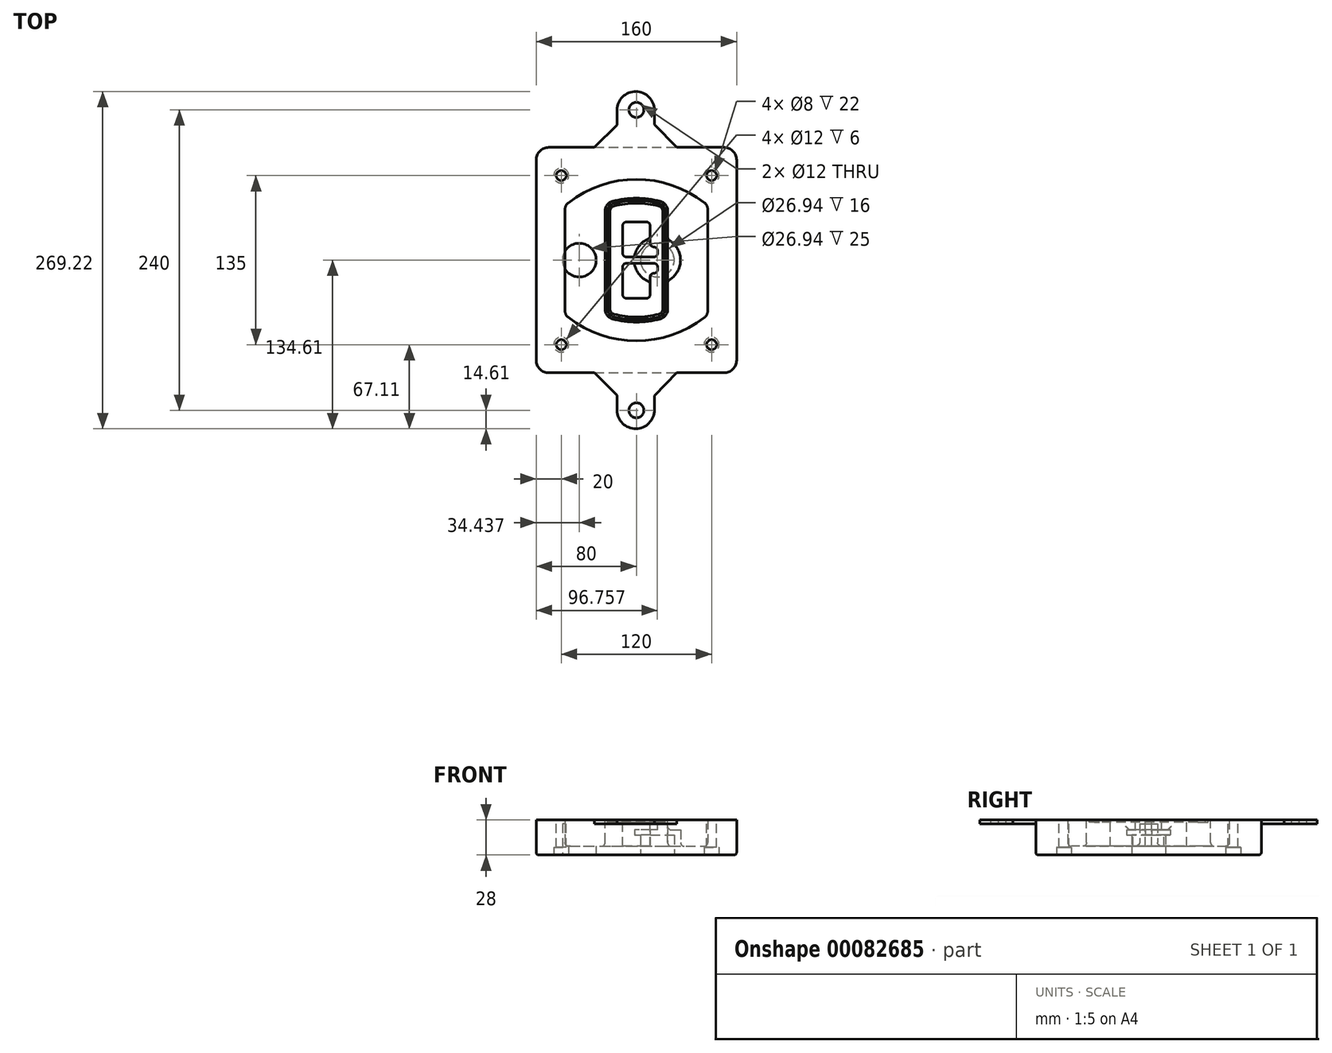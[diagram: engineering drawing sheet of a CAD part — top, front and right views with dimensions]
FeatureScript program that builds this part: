
annotation { "Feature Type Name" : "Feature", "Feature Type Description" : "" }
export const myFeature = defineFeature(function(context is Context, id is Id, definition is map)
    precondition{}
    {
        {
            var Q0;
            Q0=qCreatedBy(makeId("Top.planeOp"),FACE);
            var sketch = newSketch(context, id + "F0", { "sketchPlane" : qUnion([Q0])});
            skPoint(sketch, "E0.rect.middle", {"position": v(0, 0) * mm});
            skLineSegment(sketch, "E1.bottom", {"start": v(-70, -90) * mm, "end": v(70, -90) * mm});
            skLineSegment(sketch, "E1.top", {"start": v(-70, 90) * mm, "end": v(70, 90) * mm});
            skLineSegment(sketch, "E1.left", {"start": v(-80, -80) * mm, "end": v(-80, 80) * mm});
            skLineSegment(sketch, "E1.right", {"start": v(80, -80) * mm, "end": v(80, 80) * mm});
            skLineSegment(sketch, "E2", {"start": v(-80, 90) * mm, "end": v(80, -90) * mm, "construction": true});
            skLineSegment(sketch, "E3", {"start": v(80, 90) * mm, "end": v(-80, -90) * mm, "construction": true});
            skCircle(sketch, "E4", {"center": v(-60, 67.5) * mm, "radius": 4 * mm});
            skCircle(sketch, "E5", {"center": v(60, 67.5) * mm, "radius": 4 * mm});
            skCircle(sketch, "E6", {"center": v(60, -67.5) * mm, "radius": 4 * mm});
            skCircle(sketch, "E7", {"center": v(-60, -67.5) * mm, "radius": 4 * mm});
            skLineSegment(sketch, "E8", {"start": v(-60, 67.5) * mm, "end": v(60, 67.5) * mm, "construction": true});
            skLineSegment(sketch, "E9", {"start": v(60, 67.5) * mm, "end": v(60, -67.5) * mm, "construction": true});
            skLineSegment(sketch, "E10", {"start": v(60, -67.5) * mm, "end": v(-60, -67.5) * mm, "construction": true});
            skLineSegment(sketch, "E11", {"start": v(-60, -67.5) * mm, "end": v(-60, 67.5) * mm, "construction": true});
            skLineSegment(sketch, "E12", {"start": v(-60, 40.3) * mm, "end": v(-60, -40.3) * mm});
            skLineSegment(sketch, "E13", {"start": v(60, 40.3) * mm, "end": v(60, -40.3) * mm});
            skArc(sketch, "E14", {"start": v(56.15, 48.18) * mm, "mid": v(0, 67.5) * mm, "end": v(-56.15, 48.18) * mm});
            skArc(sketch, "E15", {"start": v(-56.15, -48.18) * mm, "mid": v(0, -67.5) * mm, "end": v(56.15, -48.18) * mm});
            skLineSegment(sketch, "E16", {"start": v(-60, 0) * mm, "end": v(60, 0) * mm, "construction": true});
            skPoint(sketch, "E17.visualSharp", {"position": v(-60, -45) * mm});
            skArc(sketch, "E17.filletArc", {"start": v(-60, -40.3) * mm, "mid": v(-58.99, -44.68) * mm, "end": v(-56.15, -48.18) * mm});
            skPoint(sketch, "E18.visualSharp", {"position": v(-60, 45) * mm});
            skArc(sketch, "E18.filletArc", {"start": v(-56.15, 48.18) * mm, "mid": v(-58.99, 44.68) * mm, "end": v(-60, 40.3) * mm});
            skPoint(sketch, "E19.visualSharp", {"position": v(60, 45) * mm});
            skArc(sketch, "E19.filletArc", {"start": v(60, 40.3) * mm, "mid": v(58.99, 44.68) * mm, "end": v(56.15, 48.18) * mm});
            skPoint(sketch, "E20.visualSharp", {"position": v(60, -45) * mm});
            skArc(sketch, "E20.filletArc", {"start": v(56.15, -48.18) * mm, "mid": v(58.99, -44.68) * mm, "end": v(60, -40.3) * mm});
            skPoint(sketch, "E21.visualSharp", {"position": v(-80, 90) * mm});
            skArc(sketch, "E21.filletArc", {"start": v(-70, 90) * mm, "mid": v(-77.07, 87.07) * mm, "end": v(-80, 80) * mm});
            skPoint(sketch, "E22.visualSharp", {"position": v(80, 90) * mm});
            skArc(sketch, "E22.filletArc", {"start": v(80, 80) * mm, "mid": v(77.07, 87.07) * mm, "end": v(70, 90) * mm});
            skPoint(sketch, "E23.visualSharp", {"position": v(80, -90) * mm});
            skArc(sketch, "E23.filletArc", {"start": v(70, -90) * mm, "mid": v(77.07, -87.07) * mm, "end": v(80, -80) * mm});
            skPoint(sketch, "E24.visualSharp", {"position": v(-80, -90) * mm});
            skArc(sketch, "E24.filletArc", {"start": v(-80, -80) * mm, "mid": v(-77.07, -87.07) * mm, "end": v(-70, -90) * mm});
            skArc(sketch, "E25.0", {"start": v(57, 40.3) * mm, "mid": v(56.3, 43.36) * mm, "end": v(54.3, 45.81) * mm});
            skLineSegment(sketch, "E25.1", {"start": v(57, 40.3) * mm, "end": v(57, -40.3) * mm});
            skArc(sketch, "E25.2", {"start": v(54.3, -45.81) * mm, "mid": v(56.3, -43.36) * mm, "end": v(57, -40.3) * mm});
            skArc(sketch, "E25.3", {"start": v(-54.3, -45.81) * mm, "mid": v(0, -64.5) * mm, "end": v(54.3, -45.81) * mm});
            skArc(sketch, "E25.4", {"start": v(-57, -40.3) * mm, "mid": v(-56.3, -43.36) * mm, "end": v(-54.3, -45.81) * mm});
            skArc(sketch, "E25.5", {"start": v(54.3, 45.81) * mm, "mid": v(0, 64.5) * mm, "end": v(-54.3, 45.81) * mm});
            skLineSegment(sketch, "E25.6", {"start": v(-57, 40.3) * mm, "end": v(-57, -40.3) * mm});
            skArc(sketch, "E25.7", {"start": v(-54.3, 45.81) * mm, "mid": v(-56.3, 43.36) * mm, "end": v(-57, 40.3) * mm});
            skArc(sketch, "E26.0", {"start": v(-58.62, 51.33) * mm, "mid": v(-62.58, 46.43) * mm, "end": v(-64, 40.3) * mm});
            skArc(sketch, "E26.1", {"start": v(58.62, 51.33) * mm, "mid": v(0, 71.5) * mm, "end": v(-58.62, 51.33) * mm});
            skArc(sketch, "E26.2", {"start": v(64, 40.3) * mm, "mid": v(62.58, 46.43) * mm, "end": v(58.62, 51.33) * mm});
            skLineSegment(sketch, "E26.3", {"start": v(64, 40.3) * mm, "end": v(64, -40.3) * mm});
            skArc(sketch, "E26.4", {"start": v(58.62, -51.33) * mm, "mid": v(62.58, -46.43) * mm, "end": v(64, -40.3) * mm});
            skLineSegment(sketch, "E26.5", {"start": v(-64, 40.3) * mm, "end": v(-64, -40.3) * mm});
            skArc(sketch, "E26.6", {"start": v(-58.62, -51.33) * mm, "mid": v(0, -71.5) * mm, "end": v(58.62, -51.33) * mm});
            skArc(sketch, "E26.7", {"start": v(-64, -40.3) * mm, "mid": v(-62.58, -46.43) * mm, "end": v(-58.62, -51.33) * mm});
            skSolve(sketch);
        }
        {
            var Q0;
            Q0=makeQuery(id+"F0.imprint","IMPRINT",FACE,{"disambiguationData":[TD([[makeQuery(id+"F0.imprint","IMPRINT",EDGE,{"derivedFrom":sQuery(id+"F0.wireOp",EDGE,"E1.bottom")}),1.0]])]});
            var Q1;
            Q1=makeQuery(id+"F0.imprint","IMPRINT",FACE,{"disambiguationData":[TD([[makeQuery(id+"F0.imprint","IMPRINT",EDGE,{"derivedFrom":sQuery(id+"F0.wireOp",EDGE,"E12")}),1.0]])]});
            var Q2;
            Q2=makeQuery(id+"F0.imprint","IMPRINT",FACE,{"disambiguationData":[TD([[makeQuery(id+"F0.imprint","IMPRINT",EDGE,{"derivedFrom":sQuery(id+"F0.wireOp",EDGE,"E25.0")}),1.0]])]});
            var Q3;
            Q3=makeQuery(id+"F0.imprint","IMPRINT",FACE,{"disambiguationData":[TD([[makeQuery(id+"F0.imprint","IMPRINT",EDGE,{"derivedFrom":sQuery(id+"F0.wireOp",EDGE,"E12")}),-1.0]])]});
            extrude(context, id + "F1", {"entities" : qUnion([Q0, Q1, Q2, Q3]), "oppositeDirection" : true, "depth" : 25 * mm});
        }
        {
            var Q0;
            Q0=makeQuery(id+"F0.imprint","IMPRINT",FACE,{"disambiguationData":[TD([[makeQuery(id+"F0.imprint","IMPRINT",EDGE,{"derivedFrom":sQuery(id+"F0.wireOp",EDGE,"E12")}),1.0]])]});
            extrude(context, id + "F2", {"entities" : qUnion([Q0]), "operationType" : NewBodyOperationType.ADD, "depth" : 3 * mm});
        }
        {
            var Q0;
            Q0=makeQuery(id+"F0.imprint","IMPRINT",FACE,{"disambiguationData":[TD([[makeQuery(id+"F0.imprint","IMPRINT",EDGE,{"derivedFrom":sQuery(id+"F0.wireOp",EDGE,"E25.0")}),1.0]])]});
            extrude(context, id + "F3", {"entities" : qUnion([Q0]), "operationType" : NewBodyOperationType.REMOVE, "oppositeDirection" : true, "depth" : 18 * mm});
        }
        {
            var Q0;
            Q0=makeQuery(id+"F2.opExtrude","CAP_FACE",FACE,{"disambiguationData":[OSD([sQuery(id+"F0.wireOp",EDGE,"E12"),sQuery(id+"F0.wireOp",EDGE,"E13"),sQuery(id+"F0.wireOp",EDGE,"E14"),sQuery(id+"F0.wireOp",EDGE,"E15"),sQuery(id+"F0.wireOp",EDGE,"E17.filletArc"),sQuery(id+"F0.wireOp",EDGE,"E18.filletArc"),sQuery(id+"F0.wireOp",EDGE,"E19.filletArc"),sQuery(id+"F0.wireOp",EDGE,"E20.filletArc"),sQuery(id+"F0.wireOp",EDGE,"E25.0"),sQuery(id+"F0.wireOp",EDGE,"E25.1"),sQuery(id+"F0.wireOp",EDGE,"E25.2"),sQuery(id+"F0.wireOp",EDGE,"E25.3"),sQuery(id+"F0.wireOp",EDGE,"E25.4"),sQuery(id+"F0.wireOp",EDGE,"E25.5"),sQuery(id+"F0.wireOp",EDGE,"E25.6"),sQuery(id+"F0.wireOp",EDGE,"E25.7")])],"isStart":false});
            var sketch = newSketch(context, id + "F4", { "sketchPlane" : qUnion([Q0])});
            skArc(sketch, "E27.0", {"start": v(-19.08, -46.97) * mm, "mid": v(0, -49.5) * mm, "end": v(19.08, -46.97) * mm});
            skArc(sketch, "E28.0", {"start": v(19.08, 46.97) * mm, "mid": v(0, 49.5) * mm, "end": v(-19.08, 46.97) * mm});
            skLineSegment(sketch, "E29", {"start": v(-25, 39.25) * mm, "end": v(-25, -39.25) * mm});
            skLineSegment(sketch, "E30", {"start": v(25, 39.25) * mm, "end": v(25, -39.25) * mm});
            skLineSegment(sketch, "E31", {"start": v(-25, 45.1) * mm, "end": v(25, 45.1) * mm, "construction": true});
            skLineSegment(sketch, "E32", {"start": v(-25, -45.1) * mm, "end": v(25, -45.1) * mm, "construction": true});
            skPoint(sketch, "E33.visualSharp", {"position": v(-25, 45.1) * mm});
            skArc(sketch, "E33.filletArc", {"start": v(-19.08, 46.97) * mm, "mid": v(-23.35, 44.11) * mm, "end": v(-25, 39.25) * mm});
            skPoint(sketch, "E34.visualSharp", {"position": v(25, 45.1) * mm});
            skArc(sketch, "E34.filletArc", {"start": v(25, 39.25) * mm, "mid": v(23.35, 44.11) * mm, "end": v(19.08, 46.97) * mm});
            skPoint(sketch, "E35.visualSharp", {"position": v(25, -45.1) * mm});
            skArc(sketch, "E35.filletArc", {"start": v(19.08, -46.97) * mm, "mid": v(23.35, -44.11) * mm, "end": v(25, -39.25) * mm});
            skPoint(sketch, "E36.visualSharp", {"position": v(-25, -45.1) * mm});
            skArc(sketch, "E36.filletArc", {"start": v(-25, -39.25) * mm, "mid": v(-23.35, -44.11) * mm, "end": v(-19.08, -46.97) * mm});
            skArc(sketch, "E37.0", {"start": v(54.3, 45.81) * mm, "mid": v(0, 64.5) * mm, "end": v(-54.3, 45.81) * mm});
            skArc(sketch, "E37.1", {"start": v(-54.3, 45.81) * mm, "mid": v(-56.3, 43.36) * mm, "end": v(-57, 40.3) * mm});
            skLineSegment(sketch, "E37.2", {"start": v(-57, 40.3) * mm, "end": v(-57, -40.3) * mm});
            skArc(sketch, "E37.3", {"start": v(-57, -40.3) * mm, "mid": v(-56.3, -43.36) * mm, "end": v(-54.3, -45.81) * mm});
            skArc(sketch, "E37.4", {"start": v(-54.3, -45.81) * mm, "mid": v(0, -64.5) * mm, "end": v(54.3, -45.81) * mm});
            skArc(sketch, "E37.5", {"start": v(54.3, -45.81) * mm, "mid": v(56.3, -43.36) * mm, "end": v(57, -40.3) * mm});
            skLineSegment(sketch, "E37.6", {"start": v(57, 40.3) * mm, "end": v(57, -40.3) * mm});
            skArc(sketch, "E37.7", {"start": v(57, 40.3) * mm, "mid": v(56.3, 43.36) * mm, "end": v(54.3, 45.81) * mm});
            skLineSegment(sketch, "E38.0", {"start": v(23, 39.25) * mm, "end": v(23, -39.25) * mm});
            skArc(sketch, "E38.1", {"start": v(18.56, -45.04) * mm, "mid": v(21.76, -42.9) * mm, "end": v(23, -39.25) * mm});
            skArc(sketch, "E38.2", {"start": v(-18.56, -45.04) * mm, "mid": v(0, -47.5) * mm, "end": v(18.56, -45.04) * mm});
            skArc(sketch, "E38.3", {"start": v(-23, -39.25) * mm, "mid": v(-21.76, -42.9) * mm, "end": v(-18.56, -45.04) * mm});
            skLineSegment(sketch, "E38.4", {"start": v(-23, 39.25) * mm, "end": v(-23, -39.25) * mm});
            skArc(sketch, "E38.5", {"start": v(23, 39.25) * mm, "mid": v(21.76, 42.9) * mm, "end": v(18.56, 45.04) * mm});
            skArc(sketch, "E38.6", {"start": v(-18.56, 45.04) * mm, "mid": v(-21.76, 42.9) * mm, "end": v(-23, 39.25) * mm});
            skArc(sketch, "E38.7", {"start": v(18.56, 45.04) * mm, "mid": v(0, 47.5) * mm, "end": v(-18.56, 45.04) * mm});
            skArc(sketch, "E39.0", {"start": v(21, 39.25) * mm, "mid": v(20.18, 41.68) * mm, "end": v(18.04, 43.1) * mm});
            skLineSegment(sketch, "E39.1", {"start": v(21, 39.25) * mm, "end": v(21, -39.25) * mm});
            skArc(sketch, "E39.2", {"start": v(18.04, -43.1) * mm, "mid": v(20.18, -41.68) * mm, "end": v(21, -39.25) * mm});
            skArc(sketch, "E39.3", {"start": v(-18.04, -43.1) * mm, "mid": v(0, -45.5) * mm, "end": v(18.04, -43.1) * mm});
            skArc(sketch, "E39.4", {"start": v(-21, -39.25) * mm, "mid": v(-20.18, -41.68) * mm, "end": v(-18.04, -43.1) * mm});
            skArc(sketch, "E39.5", {"start": v(18.04, 43.1) * mm, "mid": v(0, 45.5) * mm, "end": v(-18.04, 43.1) * mm});
            skLineSegment(sketch, "E39.6", {"start": v(-21, 39.25) * mm, "end": v(-21, -39.25) * mm});
            skArc(sketch, "E39.7", {"start": v(-18.04, 43.1) * mm, "mid": v(-20.18, 41.68) * mm, "end": v(-21, 39.25) * mm});
            skLineSegment(sketch, "E40", {"start": v(-25, 0) * mm, "end": v(25, 0) * mm, "construction": true});
            skLineSegment(sketch, "E41", {"start": v(-11, 5.5) * mm, "end": v(-11, 27.5) * mm});
            skLineSegment(sketch, "E42", {"start": v(-8, 30.5) * mm, "end": v(8, 30.5) * mm});
            skLineSegment(sketch, "E43", {"start": v(11, 27.5) * mm, "end": v(11, 13.5) * mm});
            skLineSegment(sketch, "E44", {"start": v(14, 10.5) * mm, "end": v(14, 10.5) * mm});
            skLineSegment(sketch, "E45", {"start": v(17, 7.5) * mm, "end": v(17, 5.5) * mm});
            skLineSegment(sketch, "E46", {"start": v(14, 2.5) * mm, "end": v(-8, 2.5) * mm});
            skPoint(sketch, "E47.visualSharp", {"position": v(-11, 30.5) * mm});
            skArc(sketch, "E47.filletArc", {"start": v(-8, 30.5) * mm, "mid": v(-10.12, 29.62) * mm, "end": v(-11, 27.5) * mm});
            skPoint(sketch, "E48.visualSharp", {"position": v(11, 30.5) * mm});
            skArc(sketch, "E48.filletArc", {"start": v(11, 27.5) * mm, "mid": v(10.12, 29.62) * mm, "end": v(8, 30.5) * mm});
            skPoint(sketch, "E49.visualSharp", {"position": v(11, 10.5) * mm});
            skArc(sketch, "E49.filletArc", {"start": v(11, 13.5) * mm, "mid": v(11.88, 11.38) * mm, "end": v(14, 10.5) * mm});
            skPoint(sketch, "E50.visualSharp", {"position": v(17, 10.5) * mm});
            skArc(sketch, "E50.filletArc", {"start": v(17, 7.5) * mm, "mid": v(16.12, 9.62) * mm, "end": v(14, 10.5) * mm});
            skPoint(sketch, "E51.visualSharp", {"position": v(17, 2.5) * mm});
            skArc(sketch, "E51.filletArc", {"start": v(14, 2.5) * mm, "mid": v(16.12, 3.38) * mm, "end": v(17, 5.5) * mm});
            skPoint(sketch, "E52.visualSharp", {"position": v(-11, 2.5) * mm});
            skArc(sketch, "E52.filletArc", {"start": v(-11, 5.5) * mm, "mid": v(-10.12, 3.38) * mm, "end": v(-8, 2.5) * mm});
            skLineSegment(sketch, "E53.0.MirrorCS", {"start": v(14, -2.5) * mm, "end": v(-8, -2.5) * mm});
            skArc(sketch, "E54.0.MirrorCS", {"start": v(-11, -5.5) * mm, "mid": v(-10.12, -3.38) * mm, "end": v(-8, -2.5) * mm});
            skLineSegment(sketch, "E55.0.MirrorCS", {"start": v(-11, -5.5) * mm, "end": v(-11, -27.5) * mm});
            skArc(sketch, "E56.0.MirrorCS", {"start": v(-8, -30.5) * mm, "mid": v(-10.12, -29.62) * mm, "end": v(-11, -27.5) * mm});
            skLineSegment(sketch, "E57.0.MirrorCS", {"start": v(-8, -30.5) * mm, "end": v(8, -30.5) * mm});
            skArc(sketch, "E58.0.MirrorCS", {"start": v(11, -27.5) * mm, "mid": v(10.12, -29.62) * mm, "end": v(8, -30.5) * mm});
            skLineSegment(sketch, "E59.0.MirrorCS", {"start": v(11, -27.5) * mm, "end": v(11, -13.5) * mm});
            skArc(sketch, "E60.0.MirrorCS", {"start": v(11, -13.5) * mm, "mid": v(11.88, -11.38) * mm, "end": v(14, -10.5) * mm});
            skArc(sketch, "E61.0.MirrorCS", {"start": v(17, -7.5) * mm, "mid": v(16.12, -9.62) * mm, "end": v(14, -10.5) * mm});
            skLineSegment(sketch, "E62.0.MirrorCS", {"start": v(17, -7.5) * mm, "end": v(17, -5.5) * mm});
            skArc(sketch, "E63.0.MirrorCS", {"start": v(14, -2.5) * mm, "mid": v(16.12, -3.38) * mm, "end": v(17, -5.5) * mm});
            skSolve(sketch);
        }
        {
            var Q0;
            Q0=makeQuery(id+"F4.imprint","IMPRINT",FACE,{"disambiguationData":[TD([[makeQuery(id+"F4.imprint","IMPRINT",EDGE,{"derivedFrom":sQuery(id+"F4.wireOp",EDGE,"E27.0")}),1.0]])]});
            var Q1;
            Q1=makeQuery(id+"F4.imprint","IMPRINT",FACE,{"disambiguationData":[TD([[makeQuery(id+"F4.imprint","IMPRINT",EDGE,{"derivedFrom":sQuery(id+"F4.wireOp",EDGE,"E38.0")}),-1.0]])]});
            var Q2;
            Q2=makeQuery(id+"F4.imprint","IMPRINT",FACE,{"disambiguationData":[TD([[makeQuery(id+"F4.imprint","IMPRINT",EDGE,{"derivedFrom":sQuery(id+"F4.wireOp",EDGE,"E39.0")}),1.0]])]});
            extrude(context, id + "F5", {"entities" : qUnion([Q0, Q1, Q2]), "operationType" : NewBodyOperationType.ADD, "endBound" : BoundingType.UP_TO_NEXT, "oppositeDirection" : true, "depth" : 25 * mm});
        }
        {
            var Q0;
            Q0=makeQuery(id+"F4.imprint","IMPRINT",FACE,{"disambiguationData":[TD([[makeQuery(id+"F4.imprint","IMPRINT",EDGE,{"derivedFrom":sQuery(id+"F4.wireOp",EDGE,"E38.0")}),-1.0]])]});
            extrude(context, id + "F6", {"entities" : qUnion([Q0]), "operationType" : NewBodyOperationType.REMOVE, "oppositeDirection" : true, "depth" : 2 * mm});
        }
        {
            var Q0;
            Q0=makeQuery(id+"F1.opExtrude","CAP_FACE",FACE,{"disambiguationData":[OSD([sQuery(id+"F0.wireOp",EDGE,"E1.bottom"),sQuery(id+"F0.wireOp",EDGE,"E1.top"),sQuery(id+"F0.wireOp",EDGE,"E1.left"),sQuery(id+"F0.wireOp",EDGE,"E1.right"),sQuery(id+"F0.wireOp",EDGE,"E4"),sQuery(id+"F0.wireOp",EDGE,"E5"),sQuery(id+"F0.wireOp",EDGE,"E6"),sQuery(id+"F0.wireOp",EDGE,"E7"),sQuery(id+"F0.wireOp",EDGE,"E21.filletArc"),sQuery(id+"F0.wireOp",EDGE,"E22.filletArc"),sQuery(id+"F0.wireOp",EDGE,"E23.filletArc"),sQuery(id+"F0.wireOp",EDGE,"E24.filletArc")])],"isStart":false});
            var sketch = newSketch(context, id + "F7", { "sketchPlane" : qUnion([Q0])});
            skCircle(sketch, "E64", {"center": v(16.76, 0) * mm, "radius": 13.47 * mm});
            skCircle(sketch, "E65", {"center": v(-45.56, 0) * mm, "radius": 13.47 * mm});
            skLineSegment(sketch, "E66", {"start": v(80, 0) * mm, "end": v(-80, 0) * mm});
            skCircle(sketch, "E67", {"center": v(16.76, 0) * mm, "radius": 18.47 * mm});
            skCircle(sketch, "E68", {"center": v(60, -67.5) * mm, "radius": 6 * mm});
            skCircle(sketch, "E69", {"center": v(-60, -67.5) * mm, "radius": 6 * mm});
            skCircle(sketch, "E70", {"center": v(-60, 67.5) * mm, "radius": 6 * mm});
            skCircle(sketch, "E71", {"center": v(60, 67.5) * mm, "radius": 6 * mm});
            skSolve(sketch);
        }
        {
            var Q0;
            {var subQ1=sQuery(id+"F7.wireOp",EDGE,"E66");var subQ4=sQuery(id+"F7.wireOp",EDGE,"E64");var subQ6=makeQuery(id+"F7.imprint","INTERSECT",VERTEX,{"disambiguationData":[OD(0.0)],"derivedFrom":[subQ4,subQ1]});Q0=makeQuery(id+"F7.imprint","IMPRINT",FACE,{"disambiguationData":[TD([[makeQuery(id+"F7.imprint","IMPRINT",EDGE,{"disambiguationData":[TD([[subQ6,-1.0]])],"derivedFrom":subQ4}),-1.0]])]});}
            var Q1;
            {var subQ0=sQuery(id+"F7.wireOp",EDGE,"E66");var subQ1=sQuery(id+"F7.wireOp",EDGE,"E64");var subQ3=makeQuery(id+"F7.imprint","INTERSECT",VERTEX,{"disambiguationData":[OD(0.0)],"derivedFrom":[subQ1,subQ0]});Q1=makeQuery(id+"F7.imprint","IMPRINT",FACE,{"disambiguationData":[TD([[makeQuery(id+"F7.imprint","IMPRINT",EDGE,{"disambiguationData":[TD([[subQ3,-1.0]])],"derivedFrom":subQ1}),1.0]])]});}
            var Q2;
            {var subQ0=sQuery(id+"F7.wireOp",EDGE,"E66");var subQ1=sQuery(id+"F7.wireOp",EDGE,"E64");var subQ3=makeQuery(id+"F7.imprint","INTERSECT",VERTEX,{"disambiguationData":[OD(0.0)],"derivedFrom":[subQ1,subQ0]});Q2=makeQuery(id+"F7.imprint","IMPRINT",FACE,{"disambiguationData":[TD([[makeQuery(id+"F7.imprint","IMPRINT",EDGE,{"disambiguationData":[TD([[subQ3,1.0]])],"derivedFrom":subQ1}),1.0]])]});}
            var Q3;
            {var subQ1=sQuery(id+"F7.wireOp",EDGE,"E66");var subQ4=sQuery(id+"F7.wireOp",EDGE,"E64");var subQ6=makeQuery(id+"F7.imprint","INTERSECT",VERTEX,{"disambiguationData":[OD(0.0)],"derivedFrom":[subQ4,subQ1]});Q3=makeQuery(id+"F7.imprint","IMPRINT",FACE,{"disambiguationData":[TD([[makeQuery(id+"F7.imprint","IMPRINT",EDGE,{"disambiguationData":[TD([[subQ6,1.0]])],"derivedFrom":subQ4}),-1.0]])]});}
            extrude(context, id + "F8", {"entities" : qUnion([Q0, Q1, Q2, Q3]), "operationType" : NewBodyOperationType.ADD, "oppositeDirection" : true, "depth" : 20 * mm});
        }
        {
            var Q0;
            {var subQ0=sQuery(id+"F7.wireOp",EDGE,"E66");var subQ1=sQuery(id+"F7.wireOp",EDGE,"E64");var subQ3=makeQuery(id+"F7.imprint","INTERSECT",VERTEX,{"disambiguationData":[OD(0.0)],"derivedFrom":[subQ1,subQ0]});Q0=makeQuery(id+"F7.imprint","IMPRINT",FACE,{"disambiguationData":[TD([[makeQuery(id+"F7.imprint","IMPRINT",EDGE,{"disambiguationData":[TD([[subQ3,-1.0]])],"derivedFrom":subQ1}),1.0]])]});}
            var Q1;
            {var subQ0=sQuery(id+"F7.wireOp",EDGE,"E66");var subQ1=sQuery(id+"F7.wireOp",EDGE,"E64");var subQ3=makeQuery(id+"F7.imprint","INTERSECT",VERTEX,{"disambiguationData":[OD(0.0)],"derivedFrom":[subQ1,subQ0]});Q1=makeQuery(id+"F7.imprint","IMPRINT",FACE,{"disambiguationData":[TD([[makeQuery(id+"F7.imprint","IMPRINT",EDGE,{"disambiguationData":[TD([[subQ3,1.0]])],"derivedFrom":subQ1}),1.0]])]});}
            extrude(context, id + "F9", {"entities" : qUnion([Q0, Q1]), "operationType" : NewBodyOperationType.REMOVE, "oppositeDirection" : true, "depth" : 16 * mm});
        }
        {
            var Q0;
            {var subQ0=sQuery(id+"F7.wireOp",EDGE,"E66");var subQ1=sQuery(id+"F7.wireOp",EDGE,"E65");var subQ3=makeQuery(id+"F7.imprint","INTERSECT",VERTEX,{"disambiguationData":[OD(0.0)],"derivedFrom":[subQ1,subQ0]});Q0=makeQuery(id+"F7.imprint","IMPRINT",FACE,{"disambiguationData":[TD([[makeQuery(id+"F7.imprint","IMPRINT",EDGE,{"disambiguationData":[TD([[subQ3,-1.0]])],"derivedFrom":subQ1}),1.0]])]});}
            var Q1;
            {var subQ0=sQuery(id+"F7.wireOp",EDGE,"E66");var subQ1=sQuery(id+"F7.wireOp",EDGE,"E65");var subQ3=makeQuery(id+"F7.imprint","INTERSECT",VERTEX,{"disambiguationData":[OD(0.0)],"derivedFrom":[subQ1,subQ0]});Q1=makeQuery(id+"F7.imprint","IMPRINT",FACE,{"disambiguationData":[TD([[makeQuery(id+"F7.imprint","IMPRINT",EDGE,{"disambiguationData":[TD([[subQ3,1.0]])],"derivedFrom":subQ1}),1.0]])]});}
            extrude(context, id + "F10", {"entities" : qUnion([Q0, Q1]), "operationType" : NewBodyOperationType.REMOVE, "oppositeDirection" : true, "depth" : 25 * mm});
        }
        {
            var Q0;
            Q0=makeQuery(id+"F7.imprint","IMPRINT",FACE,{"disambiguationData":[TD([[makeQuery(id+"F7.imprint","IMPRINT",EDGE,{"derivedFrom":sQuery(id+"F7.wireOp",EDGE,"E68")}),1.0]])]});
            var Q1;
            Q1=makeQuery(id+"F7.imprint","IMPRINT",FACE,{"disambiguationData":[TD([[makeQuery(id+"F7.imprint","IMPRINT",EDGE,{"derivedFrom":makeQuery(id+"F1.opExtrude","CAP_EDGE",EDGE,{"disambiguationData":[OSD([sQuery(id+"F0.wireOp",EDGE,"E5")])],"isStart":false})}),-1.0]])]});
            var Q2;
            Q2=makeQuery(id+"F7.imprint","IMPRINT",FACE,{"disambiguationData":[TD([[makeQuery(id+"F7.imprint","IMPRINT",EDGE,{"derivedFrom":sQuery(id+"F7.wireOp",EDGE,"E69")}),1.0]])]});
            var Q3;
            Q3=makeQuery(id+"F7.imprint","IMPRINT",FACE,{"disambiguationData":[TD([[makeQuery(id+"F7.imprint","IMPRINT",EDGE,{"derivedFrom":makeQuery(id+"F1.opExtrude","CAP_EDGE",EDGE,{"disambiguationData":[OSD([sQuery(id+"F0.wireOp",EDGE,"E4")])],"isStart":false})}),-1.0]])]});
            var Q4;
            Q4=makeQuery(id+"F7.imprint","IMPRINT",FACE,{"disambiguationData":[TD([[makeQuery(id+"F7.imprint","IMPRINT",EDGE,{"derivedFrom":sQuery(id+"F7.wireOp",EDGE,"E70")}),1.0]])]});
            var Q5;
            Q5=makeQuery(id+"F7.imprint","IMPRINT",FACE,{"disambiguationData":[TD([[makeQuery(id+"F7.imprint","IMPRINT",EDGE,{"derivedFrom":makeQuery(id+"F1.opExtrude","CAP_EDGE",EDGE,{"disambiguationData":[OSD([sQuery(id+"F0.wireOp",EDGE,"E7")])],"isStart":false})}),-1.0]])]});
            var Q6;
            Q6=makeQuery(id+"F7.imprint","IMPRINT",FACE,{"disambiguationData":[TD([[makeQuery(id+"F7.imprint","IMPRINT",EDGE,{"derivedFrom":sQuery(id+"F7.wireOp",EDGE,"E71")}),1.0]])]});
            var Q7;
            Q7=makeQuery(id+"F7.imprint","IMPRINT",FACE,{"disambiguationData":[TD([[makeQuery(id+"F7.imprint","IMPRINT",EDGE,{"derivedFrom":makeQuery(id+"F1.opExtrude","CAP_EDGE",EDGE,{"disambiguationData":[OSD([sQuery(id+"F0.wireOp",EDGE,"E6")])],"isStart":false})}),-1.0]])]});
            extrude(context, id + "F11", {"entities" : qUnion([Q0, Q1, Q2, Q3, Q4, Q5, Q6, Q7]), "operationType" : NewBodyOperationType.REMOVE, "oppositeDirection" : true, "depth" : 6 * mm});
        }
        {
            var Q0;
            Q0=makeQuery(id+"F9.boolean.opBoolean","COPY",FACE,{"derivedFrom":makeQuery(id+"F9.opExtrude","CAP_FACE",FACE,{"disambiguationData":[OSD([sQuery(id+"F7.wireOp",EDGE,"E64")])],"isStart":false})});
            var sketch = newSketch(context, id + "F12", { "sketchPlane" : qUnion([Q0])});
            skArc(sketch, "E72.0", {"start": v(11, 17.55) * mm, "mid": v(2.57, 11.82) * mm, "end": v(-1.54, 2.5) * mm});
            skArc(sketch, "E72.1", {"start": v(-1.54, -2.5) * mm, "mid": v(2.57, -11.82) * mm, "end": v(11, -17.55) * mm});
            skLineSegment(sketch, "E73", {"start": v(-1.54, -2.5) * mm, "end": v(14, -2.5) * mm});
            skLineSegment(sketch, "E74.0", {"start": v(14, 2.5) * mm, "end": v(-1.54, 2.5) * mm});
            skArc(sketch, "E74.1", {"start": v(14, 2.5) * mm, "mid": v(16.12, 3.38) * mm, "end": v(17, 5.5) * mm});
            skLineSegment(sketch, "E74.2", {"start": v(17, 7.5) * mm, "end": v(17, 5.5) * mm});
            skArc(sketch, "E74.3", {"start": v(17, 7.5) * mm, "mid": v(16.12, 9.62) * mm, "end": v(14, 10.5) * mm});
            skArc(sketch, "E74.4", {"start": v(11, 13.5) * mm, "mid": v(11.88, 11.38) * mm, "end": v(14, 10.5) * mm});
            skLineSegment(sketch, "E74.5", {"start": v(11, 17.55) * mm, "end": v(11, 13.5) * mm});
            skLineSegment(sketch, "E74.7", {"start": v(14, -2.5) * mm, "end": v(-1.54, -2.5) * mm});
            skArc(sketch, "E74.8", {"start": v(14, -2.5) * mm, "mid": v(16.12, -3.38) * mm, "end": v(17, -5.5) * mm});
            skLineSegment(sketch, "E74.9", {"start": v(17, -7.5) * mm, "end": v(17, -5.5) * mm});
            skArc(sketch, "E74.10", {"start": v(17, -7.5) * mm, "mid": v(16.12, -9.62) * mm, "end": v(14, -10.5) * mm});
            skArc(sketch, "E74.11", {"start": v(11, -13.5) * mm, "mid": v(11.88, -11.38) * mm, "end": v(14, -10.5) * mm});
            skLineSegment(sketch, "E74.12", {"start": v(11, -17.55) * mm, "end": v(11, -13.5) * mm});
            skPoint(sketch, "E75.orphan", {"position": v(11, -27.5) * mm});
            skPoint(sketch, "E76.orphan", {"position": v(-8, -2.5) * mm});
            skPoint(sketch, "E77.orphan", {"position": v(-8, 2.5) * mm});
            skPoint(sketch, "E78.orphan", {"position": v(11, 27.5) * mm});
            skSolve(sketch);
        }
        {
            var Q0;
            {var subQ7=sQuery(id+"F12.wireOp",EDGE,"E72.0");var subQ14=sQuery(id+"F12.wireOp",EDGE,"E72.1");var subQ16=sQuery(id+"F12.wireOp",EDGE,"E74.1");var subQ18=sQuery(id+"F12.wireOp",EDGE,"E74.8");Q0=qUnion([makeQuery(id+"F12.imprint","IMPRINT",FACE,{"disambiguationData":[TD([[makeQuery(id+"F12.imprint","IMPRINT",EDGE,{"derivedFrom":subQ7}),1.0]])]}),makeQuery(id+"F12.imprint","IMPRINT",FACE,{"disambiguationData":[TD([[makeQuery(id+"F12.imprint","IMPRINT",EDGE,{"derivedFrom":subQ14}),1.0]])]}),makeQuery(id+"F12.imprint","IMPRINT",FACE,{"disambiguationData":[TD([[makeQuery(id+"F12.imprint","IMPRINT",EDGE,{"derivedFrom":subQ16}),1.0]])]}),makeQuery(id+"F12.imprint","IMPRINT",FACE,{"disambiguationData":[TD([[makeQuery(id+"F12.imprint","IMPRINT",EDGE,{"derivedFrom":subQ18}),-1.0]])]})]);}
            var Q1;
            Q1=makeQuery(id+"F5.boolean.opBoolean","SPLIT",FACE,{"disambiguationData":[TD([makeQuery(id+"F5.opExtrude","SWEPT_FACE",FACE,{"disambiguationData":[OSD([sQuery(id+"F4.wireOp",EDGE,"E41")])]})])],"derivedFrom":makeQuery(id+"F3.boolean.opBoolean","COPY",FACE,{"derivedFrom":makeQuery(id+"F3.opExtrude","CAP_FACE",FACE,{"disambiguationData":[OSD([sQuery(id+"F0.wireOp",EDGE,"E25.0"),sQuery(id+"F0.wireOp",EDGE,"E25.1"),sQuery(id+"F0.wireOp",EDGE,"E25.2"),sQuery(id+"F0.wireOp",EDGE,"E25.3"),sQuery(id+"F0.wireOp",EDGE,"E25.4"),sQuery(id+"F0.wireOp",EDGE,"E25.5"),sQuery(id+"F0.wireOp",EDGE,"E25.6"),sQuery(id+"F0.wireOp",EDGE,"E25.7")])],"isStart":false})})});
            extrude(context, id + "F13", {"entities" : qUnion([Q0]), "operationType" : NewBodyOperationType.REMOVE, "endBound" : BoundingType.UP_TO_SURFACE, "endBoundEntityFace" : qUnion([Q1]), "depth" : 25 * mm});
        }
        {
            var Q0;
            Q0=makeQuery(id+"F3.boolean.opBoolean","COPY",EDGE,{"derivedFrom":makeQuery(id+"F3.opExtrude","CAP_EDGE",EDGE,{"disambiguationData":[OSD([sQuery(id+"F0.wireOp",EDGE,"E25.6")])],"isStart":false})});
            var Q1;
            Q1=makeQuery(id+"F8.boolean.opBoolean","INTERSECT",EDGE,{"derivedFrom":[makeQuery(id+"F5.opExtrude","SWEPT_FACE",FACE,{"disambiguationData":[OSD([sQuery(id+"F4.wireOp",EDGE,"E30")])]}),makeQuery(id+"F8.opExtrude","CAP_FACE",FACE,{"disambiguationData":[OSD([sQuery(id+"F7.wireOp",EDGE,"E67")])],"isStart":false})]});
            var Q2;
            Q2=makeQuery(id+"F8.boolean.opBoolean","INTERSECT",EDGE,{"disambiguationData":[OD(1.0)],"derivedFrom":[makeQuery(id+"F5.opExtrude","SWEPT_FACE",FACE,{"disambiguationData":[OSD([sQuery(id+"F4.wireOp",EDGE,"E30")])]}),makeQuery(id+"F8.opExtrude","SWEPT_FACE",FACE,{"disambiguationData":[OSD([sQuery(id+"F7.wireOp",EDGE,"E67")])]})]});
            var Q3;
            {var subQ0=sQuery(id+"F4.wireOp",EDGE,"E30");Q3=makeQuery(id+"F8.boolean.opBoolean","SPLIT",EDGE,{"disambiguationData":[TD([makeQuery(id+"F5.opExtrude","SWEPT_FACE",FACE,{"disambiguationData":[OSD([sQuery(id+"F4.wireOp",EDGE,"E35.filletArc")])]})])],"derivedFrom":makeQuery(id+"F5.opExtrude","CAP_EDGE",EDGE,{"disambiguationData":[OSD([subQ0])],"isStart":false})});}
            var Q4;
            {var subQ0=sQuery(id+"F0.wireOp",EDGE,"E25.7");var subQ1=sQuery(id+"F0.wireOp",EDGE,"E25.1");var subQ2=sQuery(id+"F0.wireOp",EDGE,"E25.6");var subQ3=sQuery(id+"F0.wireOp",EDGE,"E25.5");var subQ4=sQuery(id+"F0.wireOp",EDGE,"E25.4");var subQ5=sQuery(id+"F0.wireOp",EDGE,"E25.0");var subQ6=sQuery(id+"F0.wireOp",EDGE,"E25.2");var subQ7=sQuery(id+"F0.wireOp",EDGE,"E25.3");Q4=makeQuery(id+"F8.boolean.opBoolean","INTERSECT",EDGE,{"derivedFrom":[makeQuery(id+"F5.boolean.opBoolean","SPLIT",FACE,{"disambiguationData":[TD([makeQuery(id+"F2.opExtrude","SWEPT_FACE",FACE,{"disambiguationData":[OSD([subQ5])]})])],"derivedFrom":makeQuery(id+"F3.boolean.opBoolean","COPY",FACE,{"derivedFrom":makeQuery(id+"F3.opExtrude","CAP_FACE",FACE,{"disambiguationData":[OSD([subQ5,subQ1,subQ6,subQ7,subQ4,subQ3,subQ2,subQ0])],"isStart":false})})}),makeQuery(id+"F8.opExtrude","SWEPT_FACE",FACE,{"disambiguationData":[OSD([sQuery(id+"F7.wireOp",EDGE,"E67")])]})]});}
            var Q5;
            Q5=makeQuery(id+"F8.boolean.opBoolean","INTERSECT",EDGE,{"disambiguationData":[OD(0.0)],"derivedFrom":[makeQuery(id+"F5.opExtrude","SWEPT_FACE",FACE,{"disambiguationData":[OSD([sQuery(id+"F4.wireOp",EDGE,"E30")])]}),makeQuery(id+"F8.opExtrude","SWEPT_FACE",FACE,{"disambiguationData":[OSD([sQuery(id+"F7.wireOp",EDGE,"E67")])]})]});
            fillet(context, id + "F14", {"entities" : qUnion([Q0, Q1, Q2, Q3, Q4, Q5]), "radius" : 3 * mm, "tangentPropagation" : true, "allowEdgeOverflow" : false});
        }
        {
            var Q0;
            Q0=makeQuery(id+"F1.opExtrude","CAP_EDGE",EDGE,{"disambiguationData":[OSD([sQuery(id+"F0.wireOp",EDGE,"E1.bottom")])],"isStart":false});
            fillet(context, id + "F15", {"entities" : qUnion([Q0]), "radius" : 2 * mm, "tangentPropagation" : true, "allowEdgeOverflow" : false});
        }
        {
            var Q0;
            {var subQ0=sQuery(id+"F0.wireOp",EDGE,"E22.filletArc");var subQ1=sQuery(id+"F0.wireOp",EDGE,"E7");var subQ2=sQuery(id+"F0.wireOp",EDGE,"E6");var subQ3=sQuery(id+"F0.wireOp",EDGE,"E5");var subQ4=sQuery(id+"F0.wireOp",EDGE,"E4");var subQ5=sQuery(id+"F0.wireOp",EDGE,"E1.bottom");var subQ6=sQuery(id+"F0.wireOp",EDGE,"E21.filletArc");var subQ7=sQuery(id+"F0.wireOp",EDGE,"E1.top");var subQ8=sQuery(id+"F0.wireOp",EDGE,"E1.left");var subQ9=sQuery(id+"F0.wireOp",EDGE,"E1.right");var subQ10=sQuery(id+"F0.wireOp",EDGE,"E23.filletArc");var subQ11=sQuery(id+"F0.wireOp",EDGE,"E24.filletArc");Q0=makeQuery(id+"F2.boolean.opBoolean","SPLIT",FACE,{"disambiguationData":[TD([makeQuery(id+"F1.opExtrude","SWEPT_FACE",FACE,{"disambiguationData":[OSD([subQ5])]})])],"derivedFrom":makeQuery(id+"F1.opExtrude","CAP_FACE",FACE,{"disambiguationData":[OSD([subQ5,subQ7,subQ8,subQ9,subQ4,subQ3,subQ2,subQ1,subQ6,subQ0,subQ10,subQ11])],"isStart":true})});}
            var sketch = newSketch(context, id + "F16", { "sketchPlane" : qUnion([Q0])});
            skLineSegment(sketch, "E79", {"start": v(0, 90) * mm, "end": v(0, 120) * mm, "construction": true});
            skCircle(sketch, "E80", {"center": v(0, 120) * mm, "radius": 6 * mm});
            skLineSegment(sketch, "E81", {"start": v(-33.55, 90) * mm, "end": v(-15.55, 108) * mm});
            skLineSegment(sketch, "E82", {"start": v(32.18, 90) * mm, "end": v(14.44, 108.25) * mm});
            skLineSegment(sketch, "E83", {"start": v(-15.55, 108) * mm, "end": v(-15.55, 120) * mm});
            skLineSegment(sketch, "E84", {"start": v(14.44, 108.25) * mm, "end": v(14.44, 119.6) * mm});
            skArc(sketch, "E85", {"start": v(14.44, 119.6) * mm, "mid": v(-0.36, 134.6) * mm, "end": v(-15.55, 120) * mm});
            skLineSegment(sketch, "E86", {"start": v(-80, 0) * mm, "end": v(80, 0) * mm, "construction": true});
            skLineSegment(sketch, "E87.MirrorCS", {"start": v(-33.55, -90) * mm, "end": v(-15.55, -108) * mm});
            skLineSegment(sketch, "E88.MirrorCS", {"start": v(-15.55, -108) * mm, "end": v(-15.55, -120) * mm});
            skArc(sketch, "E89.MirrorCS", {"start": v(14.44, -119.6) * mm, "mid": v(-0.36, -134.6) * mm, "end": v(-15.55, -120) * mm});
            skCircle(sketch, "E90.MirrorC", {"center": v(0, -120) * mm, "radius": 6 * mm});
            skLineSegment(sketch, "E91.MirrorCS", {"start": v(32.18, -90) * mm, "end": v(14.44, -108.25) * mm});
            skLineSegment(sketch, "E92.MirrorCS", {"start": v(14.44, -108.25) * mm, "end": v(14.44, -119.6) * mm});
            skLineSegment(sketch, "E93.MirrorCS", {"start": v(0, -90) * mm, "end": v(0, -120) * mm, "construction": true});
            skSolve(sketch);
        }
        {
            var Q0;
            Q0=makeQuery(id+"F16.imprint","IMPRINT",FACE,{"disambiguationData":[TD([[makeQuery(id+"F16.imprint","IMPRINT",EDGE,{"derivedFrom":sQuery(id+"F16.wireOp",EDGE,"E80")}),-1.0]])]});
            var Q1;
            Q1=makeQuery(id+"F16.imprint","IMPRINT",FACE,{"disambiguationData":[TD([[makeQuery(id+"F16.imprint","IMPRINT",EDGE,{"derivedFrom":makeQuery(id+"F1.opExtrude","CAP_EDGE",EDGE,{"disambiguationData":[OSD([sQuery(id+"F0.wireOp",EDGE,"E1.left")])],"isStart":true})}),-1.0]])]});
            var Q2;
            {var subQ0=sQuery(id+"F16.wireOp",EDGE,"E87.MirrorCS");Q2=makeQuery(id+"F16.imprint","IMPRINT",FACE,{"disambiguationData":[TD([[makeQuery(id+"F16.imprint","IMPRINT",EDGE,{"derivedFrom":subQ0}),1.0]])]});}
            var Q3;
            Q3=makeQuery(id+"F2.opExtrude","CAP_FACE",FACE,{"disambiguationData":[OSD([sQuery(id+"F0.wireOp",EDGE,"E12"),sQuery(id+"F0.wireOp",EDGE,"E13"),sQuery(id+"F0.wireOp",EDGE,"E14"),sQuery(id+"F0.wireOp",EDGE,"E15"),sQuery(id+"F0.wireOp",EDGE,"E17.filletArc"),sQuery(id+"F0.wireOp",EDGE,"E18.filletArc"),sQuery(id+"F0.wireOp",EDGE,"E19.filletArc"),sQuery(id+"F0.wireOp",EDGE,"E20.filletArc"),sQuery(id+"F0.wireOp",EDGE,"E25.0"),sQuery(id+"F0.wireOp",EDGE,"E25.1"),sQuery(id+"F0.wireOp",EDGE,"E25.2"),sQuery(id+"F0.wireOp",EDGE,"E25.3"),sQuery(id+"F0.wireOp",EDGE,"E25.4"),sQuery(id+"F0.wireOp",EDGE,"E25.5"),sQuery(id+"F0.wireOp",EDGE,"E25.6"),sQuery(id+"F0.wireOp",EDGE,"E25.7")])],"isStart":false});
            extrude(context, id + "F17", {"entities" : qUnion([Q0, Q1, Q2]), "operationType" : NewBodyOperationType.ADD, "endBound" : BoundingType.UP_TO_SURFACE, "endBoundEntityFace" : qUnion([Q3]), "depth" : 25 * mm});
        }
    });
